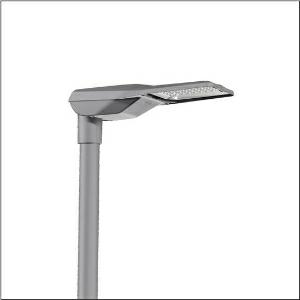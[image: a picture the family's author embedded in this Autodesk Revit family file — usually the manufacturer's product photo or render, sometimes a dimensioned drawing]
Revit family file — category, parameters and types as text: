
# Revit family: streetlight_sl_21_iq_mini___st1_0a_5xe2d21g08hb_8dd2
name_source: partatom
category: Lighting Fixtures
units: mm (PartAtom-declared; Revit-internal decimal feet)

## family parameters
Cut with Voids When Loaded = No
Host = Face
Light Source = No
Part Type = Normal
Room Calculation Point = No
Round Connector Dimension = Use Diameter
Shared = No

## types (1)
- --- (1 x LED, 7830 lm, 70.9 W, 2200K)
    Apparent Load = 71 VA
    CIE Flux Codes = 37 72 97 100 100
    Color Rendering = 70
    Color Temperature = 2200K
    Default Elevation = 1800 mm
    Description = Streetlight SL 21 iQ mini, mast luminaire, primary light control with lens, of PMMA, primary optical cover: cover, of toughened safety glass, transparent, light distribution: ST1.0a, light emission: direct distribution, primary light characteristic: asymmetric, installation type: post-top, side-entry, LED, High Power LED, rated luminous flux: 7.830lm, luminous efficacy: 110lm/W, light colour: 722, colour temperature: 2200K, control gear: iQ Street-Remote, control: Street-Remote, Auto-Match, Temp-Guard, Lumen-Switch, Night-Set, Smart-Wire, Light-Fading, Desk-Remote (wireless, voltage-free reading and setting of iQ features in the workshop via application-optimized NFC function/RFID function), optimised constant luminous flux control (CLO 2.0), pre-setting: linear dimming characteristic, mains connection: 220..240V, AC, 50/60Hz, start of lifetime: 71W, end of service life: 75W, reduction: 31W, luminaire housing, of diecast aluminium, powder-coated, Siteco® metallic grey (DB 702S), corrosivity category C5 mid according to DIN EN ISO 12944, please order mast flange separately, inclination adjustable: 0°, 5°, 10°, 15°, sealing non-destructively replaceable, multi-level sealing system, length: 628mm, width: 235mm, height: 110mm, mast flange for spigot size: 42mm (side-entry): 5XC10008XM4, 60/48mm (side-entry/post-top): 5XC10108XM2, 76/60mm (side-entry/post-top): 5XC10108XM1, mounting height: 4..8m, protection rating (complete): IP66, insulation class (complete): insulation class II (safety insulation), certification: CE, ENEC, ENEC+, VDE, impact resistance: IK10, permissible operating ambient temperature for outdoor applications: -40..+50°C, standard-compliant lighting for roads and squares, packaging unit: 1 piece

Light Distribution: ST1.0a
    Height = 110 mm
    Lamp = 1 x LED
    Lamp Light Flux = 7830 lm
    Lamp Power = 70.9 W
    Lamp count = 1
    Length = 625 mm
    Luminous efficacy = 110 lm/W
    Manufacturer = Siteco
    ModVariant = No
    Model = 5XE2D21G08HB
    Number of Poles = 1
    OnlyDefault = Yes
    Power Factor = 1
    Product Name = Streetlight SL 21 iQ mini | ST1.0a
    Product group = mast luminaire | pylon top
    ProductGroupID = 6100
    Protection Class = Protection class II
    Protection Degree = IP 66
    RLX_Detail_Level = 1
    RLX_Emergency_Light_Flux = 0 lm
    RLX_Emergency_Type = 0
    RLX_Emergency_Type_DB = No
    RlxData = <blob elided: 26261 chars, md5=ab654c07>
    Socket = socket
    Standby Power = 0 W
    System Light Flux = 7830 lm
    System Power = 71 W
    Type Comments = factory setting: luminous flux: 100 % | dim-lin: 254 | 711 mA
    Type Image = l_1003519.jpg
    URL = http://relux.com
    VarID = @adj_179743
    Voltage = 0 V
    Weight = 0.00 kg
    Width = 234 mm

## geometry (parser evidence)
native form markers: Blend x4, Sweep x10
no freeform markers — native parametric forms only
